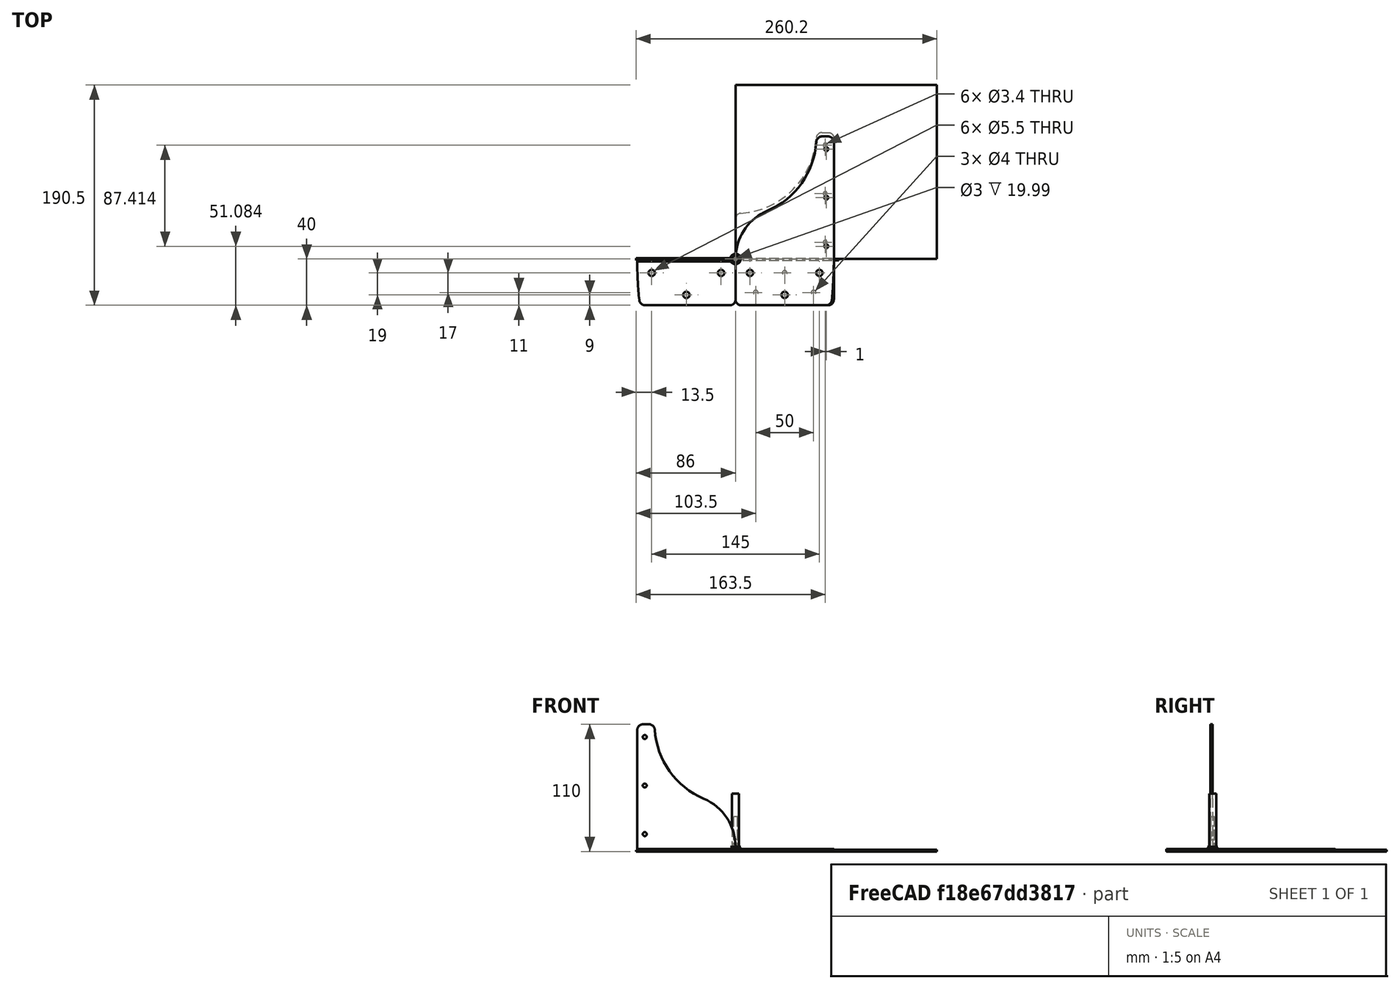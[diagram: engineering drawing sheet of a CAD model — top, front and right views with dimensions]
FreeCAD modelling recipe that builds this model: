
FCSTD DOCUMENT  (FreeCAD 0.21R31917 (Git))
Label: lamp_stand_bottom_fixture
License: All rights reserved
LicenseURL: http://en.wikipedia.org/wiki/All_rights_reserved
objects: Sketcher::SketchObject×13, Part::FeaturePython×7, Path::FeaturePython×7, TechDraw::DrawViewDimension×7, App::DocumentObjectGroup×6, PartDesign::Pocket×4, TechDraw::DrawProjGroupItem×4, Part::Feature×3, Part::Mirroring×3, App::FeaturePython×2, TechDraw::DrawSVGTemplate×2, TechDraw::DrawProjGroup×2, TechDraw::DrawPage×2, PartDesign::FeaturePython×1, PartDesign::CoordinateSystem×1, PartDesign::Fillet×1, PartDesign::Body×1, Part::Part2DObjectPython×1
note: 42 computed .brp shape members not serialized (recipe doc carries the construction recipe); baked Part::Feature solids carry a one-line shape summary decoded from their .brp

FEATURE [Sketcher::SketchObject] Sketch
  FullyConstrained = true
  MapMode = 5
  Placement = pos=(0,0,0) rot=(0.57735,0.57735,0.57735;2.0944rad)
  Support = -> [YZ_Plane]
  sketch-geometry (2):
    g0: LineSegment StartX=-40 StartY=0 StartZ=0 EndX=0 EndY=0 EndZ=0
    g1: LineSegment StartX=0 StartY=0 StartZ=0 EndX=0 EndY=110 EndZ=0
  constraints (6):
    c: PointOnObject(g0,g-1)
    c: Coincident(g0,g-1)
    c: Coincident(g0,g1)
    c: PointOnObject(g1,g-2)
    c: DistanceY(g1) = 110  'height'
    c: DistanceX(g0,g0) = 40  'length'
FEATURE [PartDesign::FeaturePython] BaseBend  # WARN: FeaturePython — macro-defined, semantics opaque (R4)
  BendSide = 1
  BendSketch = -> Sketch
  MidPlane = false
  Reverse = false
  length = 85
  radius = 2
  thickness = 2
FEATURE [Sketcher::SketchObject] Sketch001
  FullyConstrained = true
  MapMode = 5
  Placement = pos=(0,0,0) rot=(1,0,0;1.5708rad)
  Support = -> [XZ_Plane]
  expr: Constraints[1] = Sketch.Constraints.height
  expr: Constraints[5] = BaseBend.length * 2 - 15mm * 2
  sketch-geometry (4):
    g0: ArcOfCircle CenterX=0 CenterY=110 CenterZ=0 NormalX=0 NormalY=0 NormalZ=1 AngleXU=0 Radius=70 StartAngle=5.11583 EndAngle=6.28319
    g1: LineSegment StartX=0 StartY=110 StartZ=0 EndX=70 EndY=110 EndZ=0
    g2: ArcOfCircle CenterX=45.242 CenterY=4.01 CenterZ=0 NormalX=0 NormalY=0 NormalZ=1 AngleXU=0 Radius=45.242 StartAngle=1.97423 EndAngle=3.14159
    g3: LineSegment StartX=0 StartY=4.01 StartZ=0 EndX=0 EndY=110 EndZ=0
  constraints (11):
    c: PointOnObject(g0,g-2)
    c: DistanceY(g0) = 110
    c: Coincident(g1,g0)
    c: Coincident(g1,g0)
    c: Horizontal(g1)
    c: Diameter(g0) = 140
    c: Tangent(g2,g0) = 1.5708
    c: DistanceY(g2) = 4.01
    c: Coincident(g3,g0)
    c: Vertical(g3)
    c: Tangent(g3,g2) = 1.5708
FEATURE [PartDesign::Pocket] Pocket
  BaseFeature = -> BaseBend
  Direction = (0,1,2e-16)
  Length = 5
  Length2 = 5
  Midplane = true
  Profile = -> Sketch001
  ReferenceAxis = -> Sketch001 [N_Axis]
  Type = 0
FEATURE [Sketcher::SketchObject] Sketch002
  AttachmentOffset = pos=(42.5,-31,0) rot=(0,0,1;0rad)
  FullyConstrained = true
  MapMode = 5
  Placement = pos=(42.5,-31,0) rot=(0,0,1;0rad)
  Support = -> [XY_Plane]
  expr: .AttachmentOffset.Base.x = BaseBend.length / 2
  sketch-geometry (3):
    g0: Circle CenterX=0 CenterY=0 CenterZ=0 NormalX=0 NormalY=0 NormalZ=1 AngleXU=0 Radius=2.75
    g1: Circle CenterX=-30 CenterY=19 CenterZ=0 NormalX=0 NormalY=0 NormalZ=1 AngleXU=0 Radius=2.75
    g2: Circle CenterX=30 CenterY=19 CenterZ=0 NormalX=0 NormalY=0 NormalZ=1 AngleXU=0 Radius=2.75
  constraints (8):
    c: PointOnObject(g0,g-2)
    c: Symmetric(g2,g1,g-2)
    c: Equal(g0,g1)
    c: Equal(g1,g2)
    c: Diameter(g0) = 5.5
    c: DistanceX(g1,g2) = 60
    c: PointOnObject(g0,g-1)
    c: DistanceY(g2) = 19
FEATURE [Sketcher::SketchObject] Sketch003
  FullyConstrained = true
  MapMode = 5
  Placement = pos=(0,0,0) rot=(1,0,0;1.5708rad)
  Support = -> [XZ_Plane]
  expr: Constraints[4] = BaseBend.length - 6.5mm
  sketch-geometry (3):
    g0: Circle CenterX=78.5 CenterY=99 CenterZ=0 NormalX=0 NormalY=0 NormalZ=1 AngleXU=0 Radius=1.7
    g1: Circle CenterX=78.5 CenterY=15 CenterZ=0 NormalX=0 NormalY=0 NormalZ=1 AngleXU=0 Radius=1.7
    g2: Circle CenterX=78.5 CenterY=57 CenterZ=0 NormalX=0 NormalY=0 NormalZ=1 AngleXU=0 Radius=1.7
  constraints (9):
    c: Vertical(g1,g0)
    c: Equal(g1,g0)
    c: Diameter(g1) = 3.4
    c: DistanceY(g1) = 15
    c: DistanceX(g0) = 78.5
    c: DistanceY(g0) = 99
    c: Symmetric(g0,g1,g2)
    c: Equal(g2,g1)
    c: DistanceY(g1,g0) = 84
FEATURE [Sketcher::SketchObject] Sketch004
  FullyConstrained = true
  MapMode = 5
  Placement = pos=(0,0,0) rot=(1,0,0;1.5708rad)
  Support = -> [XZ_Plane]
  sketch-geometry (8):
    g0: LineSegment StartX=85 StartY=0 StartZ=0 EndX=0 EndY=0 EndZ=0
    g1: LineSegment StartX=0 StartY=0 StartZ=0 EndX=0 EndY=-12 EndZ=0
    g2: LineSegment StartX=0 StartY=-12 StartZ=0 EndX=85 EndY=-12 EndZ=0
    g3: LineSegment StartX=85 StartY=-12 StartZ=0 EndX=85 EndY=0 EndZ=0
    g4: LineSegment StartX=45 StartY=65 StartZ=0 EndX=0 EndY=65 EndZ=0
    g5: LineSegment StartX=0 StartY=65 StartZ=0 EndX=0 EndY=77 EndZ=0
    g6: LineSegment StartX=0 StartY=77 StartZ=0 EndX=45 EndY=77 EndZ=0
    g7: LineSegment StartX=45 StartY=77 StartZ=0 EndX=45 EndY=65 EndZ=0
  constraints (24):
    c: Coincident(g0,g1)
    c: Coincident(g1,g2)
    c: Coincident(g2,g3)
    c: Coincident(g3,g0)
    c: Horizontal(g0)
    c: Horizontal(g2)
    c: Vertical(g1)
    c: Vertical(g3)
    c: PointOnObject(g0,g-1)
    c: Coincident(g4,g5)
    c: Coincident(g5,g6)
    c: Coincident(g6,g7)
    c: Coincident(g7,g4)
    c: Horizontal(g4)
    c: Horizontal(g6)
    c: Vertical(g5)
    c: Vertical(g7)
    c: PointOnObject(g5,g-2)
    c: PointOnObject(g1,g-2)
    c: DistanceX(g4,g0) = 40
    c: DistanceX(g0) = 85
    c: DistanceY(g4) = 65
    c: DistanceY(g7,g7) = 12
    c: DistanceY(g2,g0) = 12
FEATURE [Part::Feature] Unfold
  shape: bbox 85 x 149.5 x 0.3367 mm, 18 faces (baked)
FEATURE [Sketcher::SketchObject] Unfold_Sketch_bends
  FullyConstrained = false
  Placement = pos=(0,-0.01183,0.0531668) rot=(1,0,0;0.21894rad)
  sketch-geometry (1):
    g0: LineSegment StartX=85 StartY=-0.244788 StartZ=0 EndX=0 EndY=-0.244788 EndZ=0
FEATURE [App::FeaturePython] SetupSheet  # Path/CAM operation (typed FeaturePython)
  ClearanceHeightExpression = OpStockZMax+SetupSheet.ClearanceHeightOffset
  ClearanceHeightOffset = 5
  CoolantMode = 0
  CoolantModes = None | Flood | Mist
  DeburrExtraDepth = 0
  DeburrWidth = 2.7
  FinalDepthExpression = 0.6 mm
  HorizRapid = 0
  ProfileDirection = 1
  ProfileprocessCircles = true
  ProfileprocessHoles = true
  ProfileprocessPerimeter = true
  SafeHeightExpression = OpStockZMax+SetupSheet.SafeHeightOffset
  SafeHeightOffset = 3
  StartDepthExpression = 3 mm
  StepDownExpression = OpToolDiameter
  VertRapid = 0
FEATURE [Part::FeaturePython] ToolBit  label="NZV6109015"  # Path/CAM toolbit (typed FeaturePython)
  BitPropertyNames = Chipload | CuttingEdgeAngle | CuttingEdgeHeight | Diameter | Flutes | Length | Material | ShankDiameter | TipDiameter
  BitShape = <path>
  Chipload = 0
  CuttingEdgeAngle = 90
  CuttingEdgeHeight = 4
  Diameter = 10
  Flutes = 0
  Length = 50
  Material = 0
  ShankDiameter = 6
  ShapeName = chamfer
  TipDiameter = 1
FEATURE [Path::FeaturePython] NZV6109015  label="NZV6109016"  # Path/CAM operation (typed FeaturePython)
  HorizFeed = 51.6667
  HorizRapid = 0
  SpindleDir = 0
  SpindleSpeed = 18000
  Tool = -> ToolBit
  ToolNumber = 2
  VertFeed = 16.6667
  VertRapid = 0
  expr: HorizRapid = SetupSheet.HorizRapid
  expr: VertRapid = SetupSheet.VertRapid
FEATURE [App::DocumentObjectGroup] Tools
  Group = -> [NZV6109015]
FEATURE [App::FeaturePython] SetupSheet001  # Path/CAM operation (typed FeaturePython)
  ClearanceHeightExpression = OpStockZMax+SetupSheet001.ClearanceHeightOffset
  ClearanceHeightOffset = 5
  CoolantMode = 0
  CoolantModes = None | Flood | Mist
  FinalDepthExpression = -0.1 mm
  HorizRapid = 0
  ProfileDirection = 1
  ProfileSide = 0
  ProfileUseComp = true
  ProfileprocessCircles = true
  ProfileprocessHoles = true
  ProfileprocessPerimeter = true
  SafeHeightExpression = OpStockZMax+SetupSheet001.SafeHeightOffset
  SafeHeightOffset = 3
  StartDepthExpression = 3 mm
  StepDownExpression = 4 mm
  VertRapid = 0
FEATURE [Part::FeaturePython] ToolBit001  label="3.175mm Endmill"  # Path/CAM toolbit (typed FeaturePython)
  BitPropertyNames = Chipload | CuttingEdgeHeight | Diameter | Flutes | Length | Material | ShankDiameter | SpindleDirection
  BitShape = <path>
  Chipload = 0
  CuttingEdgeHeight = 30
  Diameter = 3.17
  Flutes = 0
  Length = 10
  Material = 0
  ShankDiameter = 3
  ShapeName = endmill
  SpindleDirection = 0
FEATURE [Path::FeaturePython] __175mm_Endmill  label="3.175mm Endmill001"  # Path/CAM operation (typed FeaturePython)
  HorizFeed = 33.3333
  HorizRapid = 0
  SpindleDir = 0
  SpindleSpeed = 18000
  Tool = -> ToolBit001
  ToolNumber = 1
  VertFeed = 8.33333
  VertRapid = 0
  expr: HorizRapid = SetupSheet001.HorizRapid
  expr: VertRapid = SetupSheet001.VertRapid
FEATURE [App::DocumentObjectGroup] Tools001
  Group = -> [__175mm_Endmill]
FEATURE [Path::FeaturePython] Profile001  # Path/CAM operation (typed FeaturePython)
  Active = true
  AreaParams:
    Tolerance = 1e-07
    FitArcs = True
    Simplify = False
    CleanDistance = 0.0
    Accuracy = 0.01
    Unit = 1.0
    MinArcPoints = 4
    MaxArcPoints = 100
    ClipperScale = 10000000.0
    Fill = 0
    Coplanar = 0
    Reorient = True
    Outline = False
    Explode = False
    OpenMode = 0
    Deflection = 0.01
    SubjectFill = 0
    ClipFill = 0
    Offset = 1.585
    ExtraPass = 0
    Stepover = 0.0
    LastStepover = 0.0
    JoinType = 0
    EndType = 0
    MiterLimit = 2.0
    RoundPrecision = 0.0
    PocketMode = 0
    ToolRadius = 1.0
    PocketExtraOffset = 0.0
    PocketStepover = 0.0
    PocketLastStepover = 0.0
    FromCenter = False
    Angle = 45.0
    AngleShift = 0.0
    Shift = 0.0
    Thicken = False
    SectionCount = -1
    Stepdown = 1.0
    SectionOffset = 0.0
    SectionTolerance = 1e-07
    SectionMode = 2
    Project = False
  ClearanceHeight = 6.33672
  CoolantMode = 0
  CycleTime = 00:00:30
  Direction = 1
  FinalDepth = -0.1
  HandleMultipleFeatures = 0
  JoinType = 0
  MiterLimit = 0.1
  OffsetExtra = 0
  OpFinalDepth = 0
  OpStartDepth = 1.33672
  OpStockZMax = 1.33672
  OpStockZMin = 0
  OpToolDiameter = 3.17
  PathParams = {'orientation': 0, 'feedrate': 33.333333333333336, 'feedrate_v': 8.333333333333334, 'verbose': True, 'resume_height': 4.336720000001172, 'retraction': 6.336720000001172, 'return_end': True, 'preamble': False, 'start': Vector (80.56165208071131, 81.22607915370929, 6.336720000001172)}
  SafeHeight = 4.33672
  Side = 0
  SplitArcs = false
  StartDepth = 3
  StartPoint = (0,0,0)
  StepDown = 4
  ToolController = -> __175mm_Endmill
  UseComp = true
  UseStartPoint = false
  processCircles = true
  processHoles = true
  processPerimeter = true
  expr: ClearanceHeight = OpStockZMax + SetupSheet001.ClearanceHeightOffset
  expr: FinalDepth = -0.1mm
  expr: SafeHeight = OpStockZMax + SetupSheet001.SafeHeightOffset
  expr: StartDepth = 3mm
  expr: StepDown = 4mm
FEATURE [PartDesign::CoordinateSystem] Local_CS
  AttacherType = Attacher::AttachEngine3D
  AttachmentOffset = pos=(85,0,0) rot=(0,0,1;0rad)
  MapMode = 5
  Placement = pos=(85,0,0) rot=(0,0,1;0rad)
  Support = -> [XY_Plane]
  expr: .AttachmentOffset.Base.x = BaseBend.length
FEATURE [Sketcher::SketchObject] Sketch005
  FullyConstrained = true
  MapMode = 5
  Support = -> [XY_Plane]
  sketch-geometry (3):
    g0: ArcOfCircle CenterX=-269.477 CenterY=0 CenterZ=0 NormalX=0 NormalY=0 NormalZ=1 AngleXU=0 Radius=354.5 StartAngle=6.16926 EndAngle=6.2719
    g1: LineSegment StartX=82.7244 StartY=-40.3 StartZ=0 EndX=85 EndY=-40.3 EndZ=0
    g2: LineSegment StartX=85 StartY=-40.3 StartZ=0 EndX=85 EndY=-4 EndZ=0
  constraints (10):
    c: DistanceX(g0) = 85
    c: DistanceY(g0) = -4
    c: DistanceY(g0) = -40.3
    c: Perpendicular(g0,g-1)
    c: Diameter(g0) = 709
    c: Coincident(g1,g0)
    c: Horizontal(g1)
    c: Coincident(g2,g1)
    c: Coincident(g2,g0)
    c: Vertical(g2)
FEATURE [PartDesign::Pocket] Pocket003
  BaseFeature = -> Pocket
  Direction = (0,0,-1)
  Length = 5
  Length2 = 5
  Midplane = true
  Profile = -> Sketch005
  ReferenceAxis = -> Sketch005 [N_Axis]
  Type = 1
FEATURE [PartDesign::Fillet] Fillet
  Base = -> Pocket003 [Edge12,Edge15,Edge31,Edge33]
  Radius = 5
  SupportTransform = false
  UseAllEdges = false
FEATURE [PartDesign::Pocket] Pocket001
  BaseFeature = -> Fillet
  Direction = (0,0,-1)
  Length = 5
  Length2 = 5
  Midplane = true
  Profile = -> Sketch002
  ReferenceAxis = -> Sketch002 [N_Axis]
  Type = 1
FEATURE [PartDesign::Pocket] Pocket002
  BaseFeature = -> Pocket001
  Direction = (0,1,2e-16)
  Length = 5
  Length2 = 5
  Midplane = true
  Profile = -> Sketch003
  ReferenceAxis = -> Sketch003 [N_Axis]
  Type = 1
FEATURE [PartDesign::Body] Body  label="Body_material_0.30ansi"
  Group = -> [Sketch,BaseBend,Sketch001,Pocket,Sketch002,Pocket003,Fillet,Pocket001,Sketch003,Pocket002,Sketch004,Local_CS,Sketch005]
  Origin = -> Origin
  Tip = -> Pocket002
FEATURE [Part::Feature] Unfold001
  shape: bbox 85 x 149.5 x 0.3369 mm, 20 faces (baked)
FEATURE [Part::Mirroring] Part__Mirroring  label="Unfold (Mirror #1)"
  Base = (0,0,0)
  Normal = (1,0,0)
  Source = -> Unfold001
FEATURE [Part::FeaturePython] Clone001  label="Model-Unfold"  # Draft clone (typed FeaturePython)
  AttacherType = Attacher::AttachEngine3D
  Fuse = false
  Objects = -> [Unfold001]
  PathResource = Model
  Placement = pos=(88.2,40,0) rot=(0,0,1;0rad)
  Scale = (1,1,1)
FEATURE [Part::FeaturePython] Clone002  label="Model-Unfold (Mirror #1)"  # Draft clone (typed FeaturePython)
  AttacherType = Attacher::AttachEngine3D
  Fuse = false
  Objects = -> [Part__Mirroring]
  PathResource = Model
  Placement = pos=(85,40,7.2e-15) rot=(0,0,1;0rad)
  Scale = (1,1,1)
FEATURE [App::DocumentObjectGroup] Model001
  Group = -> [Clone001,Clone002]
FEATURE [Part::FeaturePython] Stock001  # WARN: FeaturePython — macro-defined, semantics opaque (R4)
  Base = -> Model001
  ExtXneg = 0
  ExtXpos = 1
  ExtYneg = 0
  ExtYpos = 1
  ExtZneg = 0
  ExtZpos = 1
  StockType = FromBase
FEATURE [Path::FeaturePython] Profile  # Path/CAM operation (typed FeaturePython)
  Active = true
  AreaParams:
    Tolerance = 1e-07
    FitArcs = True
    Simplify = False
    CleanDistance = 0.0
    Accuracy = 0.01
    Unit = 1.0
    MinArcPoints = 4
    MaxArcPoints = 100
    ClipperScale = 10000000.0
    Fill = 0
    Coplanar = 0
    Reorient = True
    Outline = False
    Explode = False
    OpenMode = 0
    Deflection = 0.01
    SubjectFill = 0
    ClipFill = 0
    Offset = -1.585
    ExtraPass = 0
    Stepover = 0.0
    LastStepover = 0.0
    JoinType = 0
    EndType = 0
    MiterLimit = 2.0
    RoundPrecision = 0.0
    PocketMode = 0
    ToolRadius = 1.0
    PocketExtraOffset = 0.0
    PocketStepover = 0.0
    PocketLastStepover = 0.0
    FromCenter = False
    Angle = 45.0
    AngleShift = 0.0
    Shift = 0.0
    Thicken = False
    SectionCount = -1
    Stepdown = 1.0
    SectionOffset = 0.0
    SectionTolerance = 1e-07
    SectionMode = 2
    Project = False
  Base = -> [Clone002,Clone001]
  ClearanceHeight = 6.33672
  CoolantMode = 0
  CycleTime = 00:00:36
  Direction = 1
  FinalDepth = -0.1
  HandleMultipleFeatures = 0
  JoinType = 0
  MiterLimit = 0.1
  OffsetExtra = 0
  OpFinalDepth = 0
  OpStartDepth = 1.33672
  OpStockZMax = 1.33672
  OpStockZMin = 0
  OpToolDiameter = 3.17
  PathParams = {'orientation': 1, 'feedrate': 33.333333333333336, 'feedrate_v': 8.333333333333334, 'verbose': True, 'resume_height': 4.336720000001172, 'retraction': 6.336720000001172, 'return_end': True, 'preamble': False, 'start': Vector (7.500268886574331, 96.60472021594934, 6.336720000001172)}
  SafeHeight = 4.33672
  Side = 0
  SplitArcs = false
  StartDepth = 3
  StartPoint = (0,0,0)
  StepDown = 4
  ToolController = -> __175mm_Endmill
  UseComp = true
  UseStartPoint = false
  processCircles = true
  processHoles = true
  processPerimeter = false
  expr: ClearanceHeight = OpStockZMax + SetupSheet001.ClearanceHeightOffset
  expr: FinalDepth = -0.1mm
  expr: SafeHeight = OpStockZMax + SetupSheet001.SafeHeightOffset
  expr: StartDepth = 3mm
  expr: StepDown = 4mm
FEATURE [App::DocumentObjectGroup] Operations001
  Group = -> [Profile,Profile001]
FEATURE [Path::FeaturePython] Job001  # Path/CAM operation (typed FeaturePython)
  CycleTime = 00:01:06
  Fixtures = G54
  GeometryTolerance = 0.01
  JobType = 0
  LastPostProcessDate = 2023-01-23 17:42:53.649442
  LastPostProcessOutput = <userpath>/2411-26D9/lamp_stand_bottom_fixture.Job001.tap
  Model = -> Model001
  Operations = -> Operations001
  OrderOutputBy = 0
  PostProcessor = 1
  PostProcessorOutputFile = %d.%j.tap
  SetupSheet = -> SetupSheet001
  SplitOutput = false
  Stock = -> Stock001
  Tools = -> Tools001
FEATURE [Sketcher::SketchObject] Unfold_Sketch_bends001
  FullyConstrained = false
  Placement = pos=(0,-0.046569,0.0975173) rot=(1,0,0;0.445523rad)
  sketch-geometry (1):
    g0: LineSegment StartX=85 StartY=-0.226295 StartZ=0 EndX=0 EndY=-0.226295 EndZ=0
FEATURE [Part::Mirroring] Part__Mirroring001  label="Unfold_Sketch_bends (Mirror #2)"
  Base = (0,0,0)
  Normal = (1,0,0)
  Source = -> Unfold_Sketch_bends001
FEATURE [Part::Part2DObjectPython] Clone2D  label="Model-Unfold_Sketch_bends"  # Draft 2D object (typed FeaturePython)
  Fuse = false
  Objects = -> [Unfold_Sketch_bends001]
  PathResource = Model
  Placement = pos=(88.2,40,0) rot=(0,0,1;0rad)
  Scale = (1,1,1)
  expr: Placement = <<Model-Unfold>>.Placement
FEATURE [Part::FeaturePython] Clone  label="Model-Unfold_Sketch_bends (Mirror #2)"  # Draft clone (typed FeaturePython)
  AttacherType = Attacher::AttachEngine3D
  Fuse = false
  Objects = -> [Part__Mirroring001]
  PathResource = Model
  Placement = pos=(85,40,7.2e-15) rot=(0,0,1;0rad)
  Scale = (1,1,1)
  expr: Placement = <<Model-Unfold (Mirror #1)>>.Placement
FEATURE [App::DocumentObjectGroup] Model
  Group = -> [Clone2D,Clone]
FEATURE [Part::FeaturePython] Stock  # WARN: FeaturePython — macro-defined, semantics opaque (R4)
  Base = -> Model
  ExtXneg = 1
  ExtXpos = 1
  ExtYneg = 1
  ExtYpos = 1
  ExtZneg = 0
  ExtZpos = 1
  Placement = pos=(-85,-0.250774,1e-16) rot=(0,0,1;0rad)
  StockType = FromBase
FEATURE [Path::FeaturePython] Engrave  # Path/CAM operation (typed FeaturePython)
  Active = true
  Base = -> [Clone,Clone2D]
  ClearanceHeight = 6
  CoolantMode = 0
  CycleTime = 00:00:11
  FinalDepth = 0.6
  OpFinalDepth = -10
  OpStartDepth = 7.2e-15
  OpStockZMax = 1
  OpStockZMin = 1e-16
  OpToolDiameter = 10
  SafeHeight = 4
  StartDepth = 3
  StartVertex = 0
  StepDown = 10
  ToolController = -> NZV6109015
  expr: ClearanceHeight = OpStockZMax + SetupSheet.ClearanceHeightOffset
  expr: FinalDepth = 0.6mm
  expr: SafeHeight = OpStockZMax + SetupSheet.SafeHeightOffset
  expr: StartDepth = 3mm
  expr: StepDown = OpToolDiameter
FEATURE [App::DocumentObjectGroup] Operations
  Group = -> [Engrave]
FEATURE [Path::FeaturePython] Job  # Path/CAM operation (typed FeaturePython)
  CycleTime = 00:00:11
  Fixtures = G54
  GeometryTolerance = 0.01
  JobType = 0
  LastPostProcessDate = 2023-01-23 17:26:49.713383
  LastPostProcessOutput = <userpath>/2411-26D9/lamp_stand_bottom_fixture.Job.tap
  Model = -> Model
  Operations = -> Operations
  OrderOutputBy = 0
  PostProcessor = 1
  PostProcessorOutputFile = %d.%j.tap
  SetupSheet = -> SetupSheet
  SplitOutput = false
  Stock = -> Stock
  Tools = -> Tools
FEATURE [Part::Feature] Unfold002
  shape: bbox 85 x 146.1 x 2.245 mm, 19 faces (baked)
FEATURE [Sketcher::SketchObject] Unfold_Sketch
  FullyConstrained = false
  sketch-geometry (17):
    g0: ArcOfCircle CenterX=5.46e-14 CenterY=106.084 CenterZ=0 NormalX=0 NormalY=0 NormalZ=1 AngleXU=-5e-16 Radius=70 StartAngle=5.11583 EndAngle=6.21647
    g1: ArcOfCircle CenterX=74.8331 CenterY=101.084 CenterZ=0 NormalX=0 NormalY=0 NormalZ=1 AngleXU=1.5708 Radius=5 StartAngle=0 EndAngle=1.50408
    g2: ArcOfCircle CenterX=45.242 CenterY=0.0940704 CenterZ=0 NormalX=0 NormalY=0 NormalZ=1 AngleXU=-5e-16 Radius=45.242 StartAngle=1.97423 EndAngle=3.14159
    g3: LineSegment StartX=74.8331 StartY=106.084 StartZ=0 EndX=80 EndY=106.084 EndZ=0
    g4: BSplineCurve PolesCount=34 KnotsCount=9 Degree=5 IsPeriodic=0
    g5: LineSegment StartX=-9.6e-15 StartY=-35 StartZ=0 EndX=3e-16 EndY=0.0940704 EndZ=0
    g6: BSplineCurve PolesCount=34 KnotsCount=9 Degree=5 IsPeriodic=0
    g7: LineSegment StartX=5 StartY=-40 StartZ=0 EndX=78.2656 EndY=-40 EndZ=0
    g8: ArcOfCircle CenterX=78.2656 CenterY=-35 CenterZ=0 NormalX=0 NormalY=0 NormalZ=1 AngleXU=-1.5708 Radius=5 StartAngle=2.7e-15 EndAngle=1.47049
    g9: ArcOfCircle CenterX=-269.477 CenterY=-4e-16 CenterZ=0 NormalX=0 NormalY=0 NormalZ=1 AngleXU=0 Radius=354.5 StartAngle=6.18287 EndAngle=6.2719
    g10: LineSegment StartX=85 StartY=-4 StartZ=0 EndX=85 EndY=101.084 EndZ=0
    g11: Circle CenterX=72.5 CenterY=-12 CenterZ=0 NormalX=0 NormalY=0 NormalZ=1 AngleXU=0 Radius=2.75
    g12: Circle CenterX=42.5 CenterY=-31 CenterZ=0 NormalX=0 NormalY=0 NormalZ=1 AngleXU=0 Radius=2.75
    g13: Circle CenterX=12.5 CenterY=-12 CenterZ=0 NormalX=0 NormalY=0 NormalZ=1 AngleXU=0 Radius=2.75
    g14: Circle CenterX=78.5 CenterY=53.0841 CenterZ=0 NormalX=0 NormalY=0 NormalZ=1 AngleXU=-5e-16 Radius=1.7
    g15: Circle CenterX=78.5 CenterY=95.0841 CenterZ=0 NormalX=0 NormalY=0 NormalZ=1 AngleXU=-5e-16 Radius=1.7
    g16: Circle CenterX=78.5 CenterY=11.0841 CenterZ=0 NormalX=0 NormalY=0 NormalZ=1 AngleXU=-5e-16 Radius=1.7
FEATURE [Sketcher::SketchObject] Unfold_Sketch_Outline
  FullyConstrained = false
  sketch-geometry (11):
    g0: ArcOfCircle CenterX=5.46e-14 CenterY=106.084 CenterZ=0 NormalX=0 NormalY=0 NormalZ=1 AngleXU=-5e-16 Radius=70 StartAngle=5.11583 EndAngle=6.21647
    g1: ArcOfCircle CenterX=74.8331 CenterY=101.084 CenterZ=0 NormalX=0 NormalY=0 NormalZ=1 AngleXU=1.5708 Radius=5 StartAngle=0 EndAngle=1.50408
    g2: LineSegment StartX=74.8331 StartY=106.084 StartZ=0 EndX=80 EndY=106.084 EndZ=0
    g3: BSplineCurve PolesCount=34 KnotsCount=9 Degree=5 IsPeriodic=0
    g4: LineSegment StartX=85 StartY=-4 StartZ=0 EndX=85 EndY=101.084 EndZ=0
    g5: ArcOfCircle CenterX=-269.477 CenterY=-4e-16 CenterZ=0 NormalX=0 NormalY=0 NormalZ=1 AngleXU=0 Radius=354.5 StartAngle=6.18287 EndAngle=6.2719
    g6: ArcOfCircle CenterX=78.2656 CenterY=-35 CenterZ=0 NormalX=0 NormalY=0 NormalZ=1 AngleXU=-1.5708 Radius=5 StartAngle=2.7e-15 EndAngle=1.47049
    g7: LineSegment StartX=5 StartY=-40 StartZ=0 EndX=78.2656 EndY=-40 EndZ=0
    g8: BSplineCurve PolesCount=34 KnotsCount=9 Degree=5 IsPeriodic=0
    g9: LineSegment StartX=-9.6e-15 StartY=-35 StartZ=0 EndX=3e-16 EndY=0.0940704 EndZ=0
    g10: ArcOfCircle CenterX=45.242 CenterY=0.0940704 CenterZ=0 NormalX=0 NormalY=0 NormalZ=1 AngleXU=-5e-16 Radius=45.242 StartAngle=1.97423 EndAngle=3.14159
FEATURE [Sketcher::SketchObject] Unfold_Sketch_Internal
  FullyConstrained = false
  sketch-geometry (6):
    g0: Circle CenterX=42.5 CenterY=-31 CenterZ=0 NormalX=0 NormalY=0 NormalZ=1 AngleXU=0 Radius=2.75
    g1: Circle CenterX=12.5 CenterY=-12 CenterZ=0 NormalX=0 NormalY=0 NormalZ=1 AngleXU=0 Radius=2.75
    g2: Circle CenterX=72.5 CenterY=-12 CenterZ=0 NormalX=0 NormalY=0 NormalZ=1 AngleXU=0 Radius=2.75
    g3: Circle CenterX=78.5 CenterY=95.0841 CenterZ=0 NormalX=0 NormalY=0 NormalZ=1 AngleXU=-5e-16 Radius=1.7
    g4: Circle CenterX=78.5 CenterY=53.0841 CenterZ=0 NormalX=0 NormalY=0 NormalZ=1 AngleXU=-5e-16 Radius=1.7
    g5: Circle CenterX=78.5 CenterY=11.0841 CenterZ=0 NormalX=0 NormalY=0 NormalZ=1 AngleXU=-5e-16 Radius=1.7
FEATURE [Sketcher::SketchObject] Unfold_Sketch_bends002
  FullyConstrained = false
  Placement = pos=(0,-0.350175,0.750338) rot=(1,0,0;0.436646rad)
  sketch-geometry (1):
    g0: LineSegment StartX=85 StartY=-1.77426 StartZ=0 EndX=0 EndY=-1.77426 EndZ=0
FEATURE [Sketcher::SketchObject] MirroredSketch
  FullyConstrained = false
  sketch-geometry (17):
    g0: ArcOfCircle CenterX=-5.46e-14 CenterY=106.084 CenterZ=0 NormalX=0 NormalY=0 NormalZ=1 AngleXU=-5e-16 Radius=70 StartAngle=3.20831 EndAngle=4.30895
    g1: ArcOfCircle CenterX=-74.8331 CenterY=101.084 CenterZ=0 NormalX=0 NormalY=0 NormalZ=1 AngleXU=1.5708 Radius=5 StartAngle=4.77911 EndAngle=6.28319
    g2: ArcOfCircle CenterX=-45.242 CenterY=0.0940704 CenterZ=0 NormalX=0 NormalY=0 NormalZ=1 AngleXU=-5e-16 Radius=45.242 StartAngle=1.1e-15 EndAngle=1.16736
    g3: LineSegment StartX=-74.8331 StartY=106.084 StartZ=0 EndX=-80 EndY=106.084 EndZ=0
    g4: BSplineCurve PolesCount=34 KnotsCount=9 Degree=5 IsPeriodic=0
    g5: LineSegment StartX=9.6e-15 StartY=-35 StartZ=0 EndX=-3e-16 EndY=0.0940704 EndZ=0
    g6: BSplineCurve PolesCount=34 KnotsCount=9 Degree=5 IsPeriodic=0
    g7: LineSegment StartX=-5 StartY=-40 StartZ=0 EndX=-78.2656 EndY=-40 EndZ=0
    g8: ArcOfCircle CenterX=-78.2656 CenterY=-35 CenterZ=0 NormalX=0 NormalY=0 NormalZ=1 AngleXU=-1.5708 Radius=5 StartAngle=4.8127 EndAngle=6.28319
    g9: ArcOfCircle CenterX=269.477 CenterY=-4e-16 CenterZ=0 NormalX=0 NormalY=0 NormalZ=1 AngleXU=0 Radius=354.5 StartAngle=3.15288 EndAngle=3.2419
    g10: LineSegment StartX=-85 StartY=-4 StartZ=0 EndX=-85 EndY=101.084 EndZ=0
    g11: Circle CenterX=-72.5 CenterY=-12 CenterZ=0 NormalX=0 NormalY=0 NormalZ=1 AngleXU=0 Radius=2.75
    g12: Circle CenterX=-42.5 CenterY=-31 CenterZ=0 NormalX=0 NormalY=0 NormalZ=1 AngleXU=0 Radius=2.75
    g13: Circle CenterX=-12.5 CenterY=-12 CenterZ=0 NormalX=0 NormalY=0 NormalZ=1 AngleXU=0 Radius=2.75
    g14: Circle CenterX=-78.5 CenterY=53.0841 CenterZ=0 NormalX=0 NormalY=0 NormalZ=1 AngleXU=-5e-16 Radius=1.7
    g15: Circle CenterX=-78.5 CenterY=95.0841 CenterZ=0 NormalX=0 NormalY=0 NormalZ=1 AngleXU=-5e-16 Radius=1.7
    g16: Circle CenterX=-78.5 CenterY=11.0841 CenterZ=0 NormalX=0 NormalY=0 NormalZ=1 AngleXU=-5e-16 Radius=1.7
FEATURE [TechDraw::DrawSVGTemplate] Template
  EditableTexts = Designed_by_Name=Designed by Name; Drawing_number=Drawing number; FC-Date=Date; FC-SC=Scale; FC-SH=Sheet; FC-Title=Title; Subtitle=Subtitle; Weight=Weight
  Height = 210
  Orientation = 1
  Template = <path>
  Width = 297
FEATURE [TechDraw::DrawProjGroupItem] ProjItem
  CoarseView = false
  Direction = (0,-1,0)
  Focus = 100
  HardHidden = false
  IsoCount = 0
  IsoHidden = false
  IsoVisible = false
  LockPosition = true
  Perspective = false
  Rotation = 0
  RotationVector = (1,0,0)
  ScaleType = 2
  SeamHidden = false
  SeamVisible = true
  SmoothHidden = false
  SmoothVisible = true
  Source = -> [Body]
  Type = 0
  X = 0
  XDirection = (1,0,0)
  Y = 0
FEATURE [TechDraw::DrawProjGroupItem] ProjItem001
  CoarseView = false
  Direction = (1,-1e-16,0)
  Focus = 100
  HardHidden = false
  IsoCount = 0
  IsoHidden = false
  IsoVisible = false
  LockPosition = false
  Perspective = false
  Rotation = 0
  RotationVector = (1,0,0)
  ScaleType = 2
  SeamHidden = false
  SeamVisible = true
  SmoothHidden = false
  SmoothVisible = true
  Source = -> [Body]
  Type = 2
  X = -77.5
  XDirection = (1e-16,1,0)
  Y = 0
FEATURE [TechDraw::DrawProjGroup] ProjGroup
  Anchor = -> ProjItem
  AutoDistribute = true
  LockPosition = false
  ProjectionType = 0
  Rotation = 0
  ScaleType = 0
  Source = -> [Body]
  Views = -> [ProjItem,ProjItem001]
  X = 148.5
  Y = 121
  spacingX = 15
  spacingY = 15
FEATURE [TechDraw::DrawViewDimension] Dimension
  AngleOverride = false
  Arbitrary = false
  ArbitraryTolerances = false
  EqualTolerance = true
  ExtensionAngle = 0
  FormatSpec = R%.2w
  FormatSpecOverTolerance = %+.2w
  FormatSpecUnderTolerance = %+.2w
  Inverted = false
  LineAngle = 0
  LockPosition = false
  MeasureType = 1
  OverTolerance = 0
  References2D = -> [ProjItem001]
  Rotation = 0
  ScaleType = 0
  TheoreticalExact = false
  Type = 4
  UnderTolerance = 0
  X = 11.4927
  Y = -41.0879
FEATURE [TechDraw::DrawViewDimension] Dimension001
  AngleOverride = false
  Arbitrary = false
  ArbitraryTolerances = false
  EqualTolerance = true
  ExtensionAngle = 0
  FormatSpec = %.2w
  FormatSpecOverTolerance = %+.2w
  FormatSpecUnderTolerance = %+.2w
  Inverted = false
  LineAngle = 0
  LockPosition = false
  MeasureType = 1
  OverTolerance = 0
  References2D = -> [ProjItem001]
  Rotation = 0
  ScaleType = 0
  TheoreticalExact = false
  Type = 1
  UnderTolerance = 0
  X = 1.98212
  Y = -56.2013
FEATURE [TechDraw::DrawViewDimension] Dimension002
  AngleOverride = false
  Arbitrary = false
  ArbitraryTolerances = false
  EqualTolerance = true
  ExtensionAngle = 0
  FormatSpec = %.2w
  FormatSpecOverTolerance = %+.2w
  FormatSpecUnderTolerance = %+.2w
  Inverted = false
  LineAngle = 0
  LockPosition = false
  MeasureType = 1
  OverTolerance = 0
  References2D = -> [ProjItem001]
  Rotation = 0
  ScaleType = 0
  TheoreticalExact = false
  Type = 2
  UnderTolerance = 0
  X = 0
  Y = 0
FEATURE [TechDraw::DrawViewDimension] Dimension003
  AngleOverride = false
  Arbitrary = false
  ArbitraryTolerances = false
  EqualTolerance = true
  ExtensionAngle = 0
  FormatSpec = %.2w
  FormatSpecOverTolerance = %+.2w
  FormatSpecUnderTolerance = %+.2w
  Inverted = false
  LineAngle = 0
  LockPosition = false
  MeasureType = 1
  OverTolerance = 0
  References2D = -> [ProjItem]
  Rotation = 0
  ScaleType = 0
  TheoreticalExact = false
  Type = 1
  UnderTolerance = 0
  X = -0.470507
  Y = -55.7912
FEATURE [TechDraw::DrawPage] Page
  KeepUpdated = true
  NextBalloonIndex = 1
  ProjectionType = 0
  Template = -> Template
  Views = -> [ProjGroup,Dimension,Dimension001,Dimension002,Dimension003]
FEATURE [Part::Mirroring] Part__Mirroring002  label="Body_material_0.30ansi (Mirror #3)"
  Base = (0,0,0)
  Normal = (1,0,0)
  Source = -> Body
FEATURE [TechDraw::DrawSVGTemplate] Template001
  EditableTexts = Designed_by_Name=Designed by Name; Drawing_number=Drawing number; FC-Date=Date; FC-SC=Scale; FC-SH=Sheet; FC-Title=Title; Subtitle=Subtitle; Weight=Weight
  Height = 210
  Orientation = 1
  Template = <path>
  Width = 297
FEATURE [TechDraw::DrawProjGroupItem] ProjItem002
  CoarseView = false
  Direction = (0,-1,0)
  Focus = 100
  HardHidden = false
  IsoCount = 0
  IsoHidden = false
  IsoVisible = false
  LockPosition = true
  Perspective = false
  Rotation = 0
  RotationVector = (1,0,0)
  ScaleType = 2
  SeamHidden = false
  SeamVisible = true
  SmoothHidden = false
  SmoothVisible = true
  Source = -> [Part__Mirroring002]
  Type = 0
  X = 0
  XDirection = (1,0,0)
  Y = 0
FEATURE [TechDraw::DrawProjGroupItem] ProjItem003
  CoarseView = false
  Direction = (1,-1e-16,0)
  Focus = 100
  HardHidden = false
  IsoCount = 0
  IsoHidden = false
  IsoVisible = false
  LockPosition = false
  Perspective = false
  Rotation = 0
  RotationVector = (1,0,0)
  ScaleType = 2
  SeamHidden = false
  SeamVisible = true
  SmoothHidden = false
  SmoothVisible = true
  Source = -> [Part__Mirroring002]
  Type = 2
  X = -77.5
  XDirection = (1e-16,1,0)
  Y = 0
FEATURE [TechDraw::DrawProjGroup] ProjGroup001
  Anchor = -> ProjItem002
  AutoDistribute = true
  LockPosition = false
  ProjectionType = 0
  Rotation = 0
  ScaleType = 0
  Source = -> [Part__Mirroring002]
  Views = -> [ProjItem002,ProjItem003]
  X = 148.5
  Y = 127
  spacingX = 15
  spacingY = 15
FEATURE [TechDraw::DrawViewDimension] Dimension004
  AngleOverride = false
  Arbitrary = false
  ArbitraryTolerances = false
  EqualTolerance = true
  ExtensionAngle = 0
  FormatSpec = %.2w
  FormatSpecOverTolerance = %+.2w
  FormatSpecUnderTolerance = %+.2w
  Inverted = false
  LineAngle = 0
  LockPosition = false
  MeasureType = 1
  OverTolerance = 0
  References2D = -> [ProjItem003]
  Rotation = 0
  ScaleType = 0
  TheoreticalExact = false
  Type = 1
  UnderTolerance = 0
  X = 0.722987
  Y = -55.7328
FEATURE [TechDraw::DrawViewDimension] Dimension005
  AngleOverride = false
  Arbitrary = false
  ArbitraryTolerances = false
  EqualTolerance = true
  ExtensionAngle = 0
  FormatSpec = %.2w
  FormatSpecOverTolerance = %+.2w
  FormatSpecUnderTolerance = %+.2w
  Inverted = false
  LineAngle = 0
  LockPosition = false
  MeasureType = 1
  OverTolerance = 0
  References2D = -> [ProjItem003]
  Rotation = 0
  ScaleType = 0
  TheoreticalExact = false
  Type = 2
  UnderTolerance = 0
  X = 25.9749
  Y = -1.10188
FEATURE [TechDraw::DrawViewDimension] Dimension006
  AngleOverride = false
  Arbitrary = false
  ArbitraryTolerances = false
  EqualTolerance = true
  ExtensionAngle = 0
  FormatSpec = R%.2w
  FormatSpecOverTolerance = %+.2w
  FormatSpecUnderTolerance = %+.2w
  Inverted = false
  LineAngle = 0
  LockPosition = false
  MeasureType = 1
  OverTolerance = 0
  References2D = -> [ProjItem003]
  Rotation = 0
  ScaleType = 0
  TheoreticalExact = false
  Type = 4
  UnderTolerance = 0
  X = 9.22678
  Y = -43.0156
FEATURE [TechDraw::DrawPage] Page001
  KeepUpdated = true
  NextBalloonIndex = 1
  ProjectionType = 0
  Template = -> Template001
  Views = -> [ProjGroup001,Dimension004,Dimension005,Dimension006]
note: 4 file-system paths scrubbed to <path> (originals preserved in the JSON sidecar)
